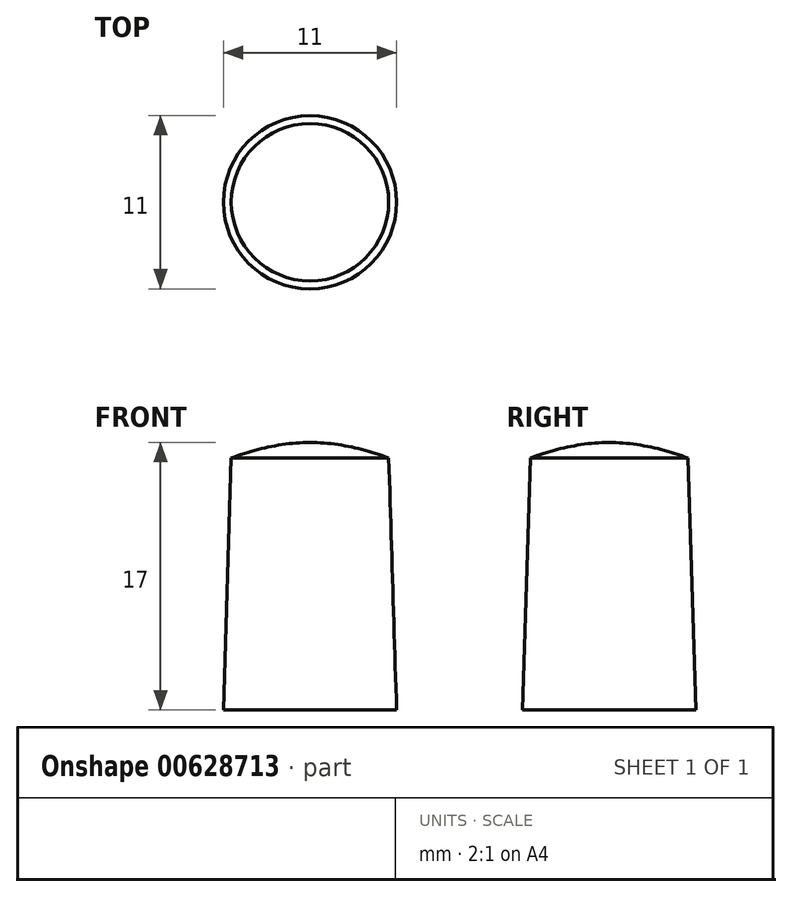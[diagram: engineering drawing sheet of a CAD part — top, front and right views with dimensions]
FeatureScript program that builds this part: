
annotation { "Feature Type Name" : "Feature", "Feature Type Description" : "" }
export const myFeature = defineFeature(function(context is Context, id is Id, definition is map)
    precondition{}
    {
        {
            var Q0;
            Q0=qCreatedBy(makeId("Front.planeOp"),FACE);
            var sketch = newSketch(context, id + "F0", { "sketchPlane" : qUnion([Q0])});
            skLineSegment(sketch, "E0", {"start": v(0, 13.97) * mm, "end": v(0, -20.72) * mm, "construction": true});
            skLineSegment(sketch, "E1", {"start": v(0, -8.5) * mm, "end": v(-5.5, -8.5) * mm});
            skLineSegment(sketch, "E2", {"start": v(-5.5, -8.5) * mm, "end": v(-5, 7.5) * mm});
            skLineSegment(sketch, "E3", {"start": v(0, -8.5) * mm, "end": v(0, 8.5) * mm});
            skArc(sketch, "E4", {"start": v(0, 8.5) * mm, "mid": v(-2.54, 8.22) * mm, "end": v(-5, 7.5) * mm});
            skSolve(sketch);
        }
        {
            var Q0;
            Q0 = qSketchRegion(id + "F0", true);
            var Q1;
            Q1=sQuery(id+"F0.wireOp",EDGE,"E0");
            revolve(context, id + "F1", {"entities" : qUnion([Q0]), "axis" : qUnion([Q1]), "revolveType" : RevolveType.FULL});
        }
    });
